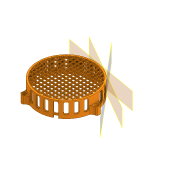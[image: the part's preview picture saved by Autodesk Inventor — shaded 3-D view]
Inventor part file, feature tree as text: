
AUTODESK INVENTOR PART (.ipt)
format: ipt  version: 2020.3 (Build 243373000, 373)  size: 1,351,680 bytes
history: native  units: mm
features: other x23, extrude x10, sketch x7, plane x3, pattern_circular x3
ambient origin geometry x8: Origin, YZ Plane, XZ Plane, XY Plane, X Axis, Y Axis, Z Axis, Center Point
bodies: Body1 (feature_tree)
feature tree (46):
  sketch  "Sketch1"  dims[d0=95.0mm d1=120.0deg]
  extrude  "Extrusion9"  TaperAngle=120.0deg  [1 undecoded]
  extrude  "Extrusion13"  Depth=16.0mm
  extrude  "Extrusion14"  Depth=6.5mm
  extrude  "Extrusion16"  Depth=10.0mm
  extrude  "Extrusion17"  Depth=1.2mm
  plane  "Work Plane5"
  plane  "Work Plane6"
  plane  "Work Plane7"
  sketch  "Sketch12"  dims[d4=3.4mm d5=6.5mm]
  sketch  "Sketch13"  dims[d7=10.0mm d8=3.6mm]
  sketch  "Sketch14"  dims[d9=2.4mm d10=1.2mm]
  extrude  "Extrusion21"  Depth=9.8mm
  extrude  "Extrusion22"  Depth=2.0mm
  extrude  "Extrusion23"  Depth=2.0mm
  sketch  "Sketch15"  dims[d13=30.0mm d15=360.0deg d17=9.8mm]
  sketch  "Sketch16"  dims[d18=12.0mm d19=2.0mm d20=6.0mm d21=2.0mm d23=60.0deg d24=6.1mm d25=8.0mm d26=6.1mm d27=60.0deg d28=3.490659mm d29=3.490659mm d56=40.0mm d57=60.0mm d58=3.2mm d59=1.3mm d60=1.0mm d61=1.0mm d62=1.3mm d64=3.0mm d65=8.0mm d66=6.0mm d74=90.0mm d75=26.0mm d76=0.0mm d83=4.2mm d84=0.0mm d85=8.4mm d86=0.0mm d99=12.5mm d100=0.0mm d101=6.5mm d102=6.0mm d103=6.0mm d104=3.0mm d105=0.0mm d115=4.0mm d116=4.0mm d122=90.0deg d123=90.0deg d124=90.0deg d126=5.5mm d127=5.5mm d128=5.5mm d129=10.0mm d130=0.0mm d131=10.0mm d132=0.0mm d133=10.0mm d134=0.0mm d137=18.0mm d138=2.0mm d141=240.0mm d142=360.0deg d191=2.0mm d192=0.0mm d194=95.0mm d195=90.0mm d198=1.0mm d199=5.0mm d200=1.0mm d201=5.0mm d202=1.0mm d203=5.0mm d204=1.0mm d205=5.0mm d206=1.0mm d207=5.0mm d208=1.0mm d209=5.0mm d210=1.0mm d211=1.0mm d212=5.0mm d213=1.0mm d214=5.0mm d215=1.0mm d216=5.0mm d217=1.0mm d218=5.0mm d219=1.0mm d220=5.0mm d221=1.0mm d222=5.0mm d223=1.0mm d224=5.0mm d225=1.0mm d226=40.0mm d227=360.0deg d229=6.1mm d230=6.0mm d231=0.0mm d232=240.0mm d233=360.0deg d72=0.5mm d73=0.872665mm d106=0.5mm d107=0.872665mm d108=0.5mm d109=0.872665mm d120=0.5mm d121=0.872665mm d125=0.872665mm d139=0.5mm d140=0.872665mm]
  pattern_circular  "Circular Pattern3"  [2 undecoded]
  extrude  "Extrusion27"  TaperAngle=60.0deg  [1 undecoded]
  pattern_circular  "Circular Pattern5"  [2 undecoded]
  extrude  "Extrusion28"  Depth=2.0mm
  pattern_circular  "Circular Pattern6"  [2 undecoded]
  sketch  "Sketch8"  dims[d2=120.0deg d3=16.0mm]
  other  "Work Axis1"
  other  "Work Axis2"
  other  "Work Axis3"
  other  "Work Axis4"
  other  "Work Axis5"
  other  "Work Axis6"
  other  "Work Axis7"
  other  "Work Axis8"
  other  "Work Axis9"
  other  "Work Axis10"
  other  "Work Axis11"
  other  "Work Axis12"
  other  "Work Axis13"
  other  "Work Axis14"
  other  "Work Axis15"
  other  "Work Axis16"
  other  "Work Axis17"
  other  "Work Axis18"
  other  "Work Axis19"
  other  "Work Axis20"
  other  "Work Axis21"
  other  "Work Axis22"
  other  "Work Axis23"
note: 8 required parameter values undecoded (feature->parameter linkage not recoverable at this tier; creation-order binding heuristic only, values carry confidence <= 0.55)
